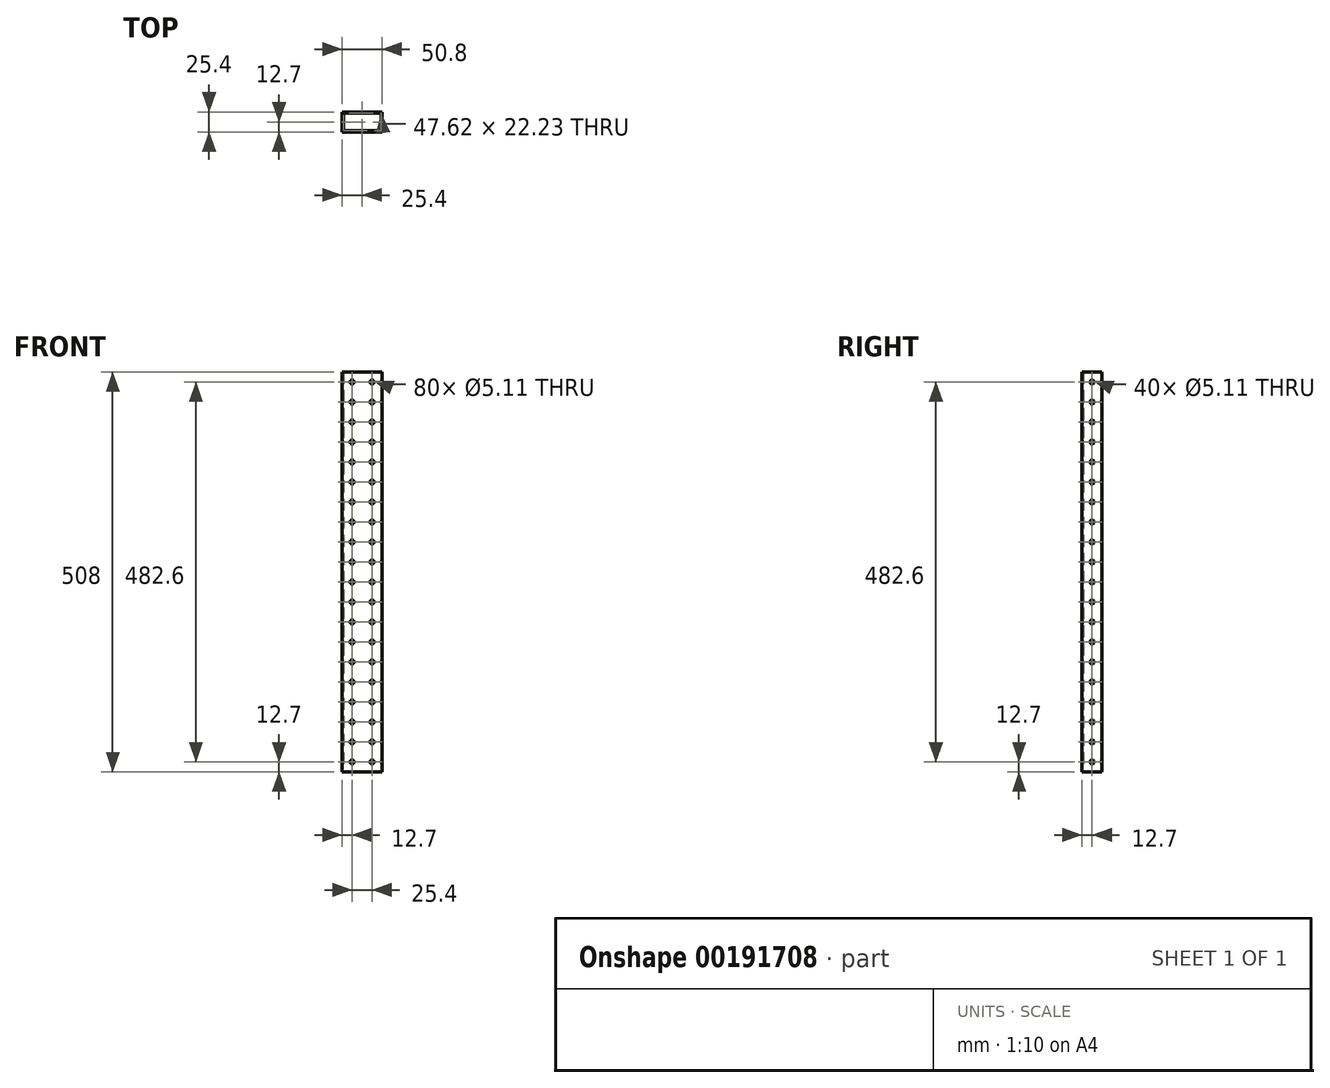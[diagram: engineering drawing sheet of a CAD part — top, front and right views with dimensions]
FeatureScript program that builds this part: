
annotation { "Feature Type Name" : "Feature", "Feature Type Description" : "" }
export const myFeature = defineFeature(function(context is Context, id is Id, definition is map)
    precondition{}
    {
        {
            var Q0;
            Q0=qCreatedBy(makeId("Top.planeOp"),FACE);
            var sketch = newSketch(context, id + "F0", { "sketchPlane" : qUnion([Q0])});
            skLineSegment(sketch, "E0.bottom", {"start": v(25.4, 12.7) * mm, "end": v(-25.4, 12.7) * mm});
            skLineSegment(sketch, "E0.top", {"start": v(25.4, -12.7) * mm, "end": v(-25.4, -12.7) * mm});
            skLineSegment(sketch, "E0.left", {"start": v(25.4, 12.7) * mm, "end": v(25.4, -12.7) * mm});
            skLineSegment(sketch, "E0.right", {"start": v(-25.4, 12.7) * mm, "end": v(-25.4, -12.7) * mm});
            skPoint(sketch, "E0.middle", {"position": v(0, 0) * mm});
            skLineSegment(sketch, "E1.bottom", {"start": v(23.81, 11.11) * mm, "end": v(-23.81, 11.11) * mm});
            skLineSegment(sketch, "E1.top", {"start": v(23.81, -11.11) * mm, "end": v(-23.81, -11.11) * mm});
            skLineSegment(sketch, "E1.left", {"start": v(23.81, 11.11) * mm, "end": v(23.81, -11.11) * mm});
            skLineSegment(sketch, "E1.right", {"start": v(-23.81, 11.11) * mm, "end": v(-23.81, -11.11) * mm});
            skSolve(sketch);
        }
        {
            var Q0;
            Q0 = qSketchRegion(id + "F0", true);
            extrude(context, id + "F1", {"entities" : qUnion([Q0]), "depth" : 508 * mm});
        }
        {
            var Q0;
            Q0=makeQuery(id+"F1.opExtrude","SWEPT_FACE",FACE,{"disambiguationData":[OSD([sQuery(id+"F0.wireOp",EDGE,"E0.top")])]});
            var sketch = newSketch(context, id + "F2", { "sketchPlane" : qUnion([Q0])});
            skCircle(sketch, "E2", {"center": v(-12.7, 12.7) * mm, "radius": 9.36 * mm});
            skCircle(sketch, "E3.0.1.0", {"center": v(-12.7, 38.1) * mm, "radius": 9.36 * mm});
            skCircle(sketch, "E3.0.2.0", {"center": v(-12.7, 63.5) * mm, "radius": 9.36 * mm});
            skCircle(sketch, "E3.0.3.0", {"center": v(-12.7, 88.9) * mm, "radius": 9.36 * mm});
            skCircle(sketch, "E3.0.4.0", {"center": v(-12.7, 114.3) * mm, "radius": 9.36 * mm});
            skCircle(sketch, "E3.0.5.0", {"center": v(-12.7, 139.7) * mm, "radius": 9.36 * mm});
            skCircle(sketch, "E3.0.6.0", {"center": v(-12.7, 165.1) * mm, "radius": 9.36 * mm});
            skCircle(sketch, "E3.0.7.0", {"center": v(-12.7, 190.5) * mm, "radius": 9.36 * mm});
            skCircle(sketch, "E3.0.8.0", {"center": v(-12.7, 215.9) * mm, "radius": 9.36 * mm});
            skCircle(sketch, "E3.0.9.0", {"center": v(-12.7, 241.3) * mm, "radius": 9.36 * mm});
            skCircle(sketch, "E3.0.10.0", {"center": v(-12.7, 266.7) * mm, "radius": 9.36 * mm});
            skCircle(sketch, "E3.0.11.0", {"center": v(-12.7, 292.1) * mm, "radius": 9.36 * mm});
            skCircle(sketch, "E3.0.12.0", {"center": v(-12.7, 317.5) * mm, "radius": 9.36 * mm});
            skCircle(sketch, "E3.0.13.0", {"center": v(-12.7, 342.9) * mm, "radius": 9.36 * mm});
            skCircle(sketch, "E3.0.14.0", {"center": v(-12.7, 368.3) * mm, "radius": 9.36 * mm});
            skCircle(sketch, "E3.0.15.0", {"center": v(-12.7, 393.7) * mm, "radius": 9.36 * mm});
            skCircle(sketch, "E3.0.16.0", {"center": v(-12.7, 419.1) * mm, "radius": 9.36 * mm});
            skCircle(sketch, "E3.0.17.0", {"center": v(-12.7, 444.5) * mm, "radius": 9.36 * mm});
            skCircle(sketch, "E3.0.18.0", {"center": v(-12.7, 469.9) * mm, "radius": 9.36 * mm});
            skCircle(sketch, "E3.1.0.0", {"center": v(12.7, 12.7) * mm, "radius": 9.36 * mm});
            skCircle(sketch, "E3.1.1.0", {"center": v(12.7, 38.1) * mm, "radius": 9.36 * mm});
            skCircle(sketch, "E3.1.2.0", {"center": v(12.7, 63.5) * mm, "radius": 9.36 * mm});
            skCircle(sketch, "E3.1.3.0", {"center": v(12.7, 88.9) * mm, "radius": 9.36 * mm});
            skCircle(sketch, "E3.1.4.0", {"center": v(12.7, 114.3) * mm, "radius": 9.36 * mm});
            skCircle(sketch, "E3.1.5.0", {"center": v(12.7, 139.7) * mm, "radius": 9.36 * mm});
            skCircle(sketch, "E3.1.6.0", {"center": v(12.7, 165.1) * mm, "radius": 9.36 * mm});
            skCircle(sketch, "E3.1.7.0", {"center": v(12.7, 190.5) * mm, "radius": 9.36 * mm});
            skCircle(sketch, "E3.1.8.0", {"center": v(12.7, 215.9) * mm, "radius": 9.36 * mm});
            skCircle(sketch, "E3.1.9.0", {"center": v(12.7, 241.3) * mm, "radius": 9.36 * mm});
            skCircle(sketch, "E3.1.10.0", {"center": v(12.7, 266.7) * mm, "radius": 9.36 * mm});
            skCircle(sketch, "E3.1.11.0", {"center": v(12.7, 292.1) * mm, "radius": 9.36 * mm});
            skCircle(sketch, "E3.1.12.0", {"center": v(12.7, 317.5) * mm, "radius": 9.36 * mm});
            skCircle(sketch, "E3.1.13.0", {"center": v(12.7, 342.9) * mm, "radius": 9.36 * mm});
            skCircle(sketch, "E3.1.14.0", {"center": v(12.7, 368.3) * mm, "radius": 9.36 * mm});
            skCircle(sketch, "E3.1.15.0", {"center": v(12.7, 393.7) * mm, "radius": 9.36 * mm});
            skCircle(sketch, "E3.1.16.0", {"center": v(12.7, 419.1) * mm, "radius": 9.36 * mm});
            skCircle(sketch, "E3.1.17.0", {"center": v(12.7, 444.5) * mm, "radius": 9.36 * mm});
            skCircle(sketch, "E3.1.18.0", {"center": v(12.7, 469.9) * mm, "radius": 9.36 * mm});
            skLineSegment(sketch, "E3.direction1", {"start": v(-12.7, 12.7) * mm, "end": v(12.7, 12.7) * mm, "construction": true});
            skLineSegment(sketch, "E3.direction2", {"start": v(-12.7, 12.7) * mm, "end": v(-12.7, 38.1) * mm, "construction": true});
            skCircle(sketch, "E4.0.0.19", {"center": v(-12.7, 495.3) * mm, "radius": 9.36 * mm});
            skCircle(sketch, "E4.0.1.19", {"center": v(12.7, 495.3) * mm, "radius": 9.36 * mm});
            skSolve(sketch);
        }
        {
            var Q0;
            Q0=sQuery(id+"F2.wireOp",VERTEX,"E3.0.12.0.center");
            var Q1;
            Q1=sQuery(id+"F2.wireOp",VERTEX,"E3.0.13.0.center");
            var Q2;
            Q2=sQuery(id+"F2.wireOp",VERTEX,"E3.1.13.0.center");
            var Q3;
            Q3=sQuery(id+"F2.wireOp",VERTEX,"E3.1.12.0.center");
            var Q4;
            Q4=sQuery(id+"F2.wireOp",VERTEX,"E3.1.11.0.center");
            var Q5;
            Q5=sQuery(id+"F2.wireOp",VERTEX,"E3.1.10.0.center");
            var Q6;
            Q6=sQuery(id+"F2.wireOp",VERTEX,"E3.0.10.0.center");
            var Q7;
            Q7=sQuery(id+"F2.wireOp",VERTEX,"E3.0.11.0.center");
            var Q8;
            Q8=sQuery(id+"F2.wireOp",VERTEX,"E3.1.4.0.center");
            var Q9;
            Q9=sQuery(id+"F2.wireOp",VERTEX,"E3.0.4.0.center");
            var Q10;
            Q10=sQuery(id+"F2.wireOp",VERTEX,"E3.0.5.0.center");
            var Q11;
            Q11=sQuery(id+"F2.wireOp",VERTEX,"E3.1.5.0.center");
            var Q12;
            Q12=sQuery(id+"F2.wireOp",VERTEX,"E3.1.6.0.center");
            var Q13;
            Q13=sQuery(id+"F2.wireOp",VERTEX,"E3.0.6.0.center");
            var Q14;
            Q14=sQuery(id+"F2.wireOp",VERTEX,"E3.0.7.0.center");
            var Q15;
            Q15=sQuery(id+"F2.wireOp",VERTEX,"E3.1.7.0.center");
            var Q16;
            Q16=sQuery(id+"F2.wireOp",VERTEX,"E3.0.8.0.center");
            var Q17;
            Q17=sQuery(id+"F2.wireOp",VERTEX,"E3.1.9.0.center");
            var Q18;
            Q18=sQuery(id+"F2.wireOp",VERTEX,"E3.0.9.0.center");
            var Q19;
            Q19=sQuery(id+"F2.wireOp",VERTEX,"E3.1.8.0.center");
            var Q20;
            Q20=sQuery(id+"F2.wireOp",VERTEX,"E3.0.16.0.center");
            var Q21;
            Q21=sQuery(id+"F2.wireOp",VERTEX,"E3.0.18.0.center");
            var Q22;
            Q22=sQuery(id+"F2.wireOp",VERTEX,"E3.1.18.0.center");
            var Q23;
            Q23=sQuery(id+"F2.wireOp",VERTEX,"E3.1.16.0.center");
            var Q24;
            Q24=sQuery(id+"F2.wireOp",VERTEX,"E3.1.17.0.center");
            var Q25;
            Q25=sQuery(id+"F2.wireOp",VERTEX,"E3.0.17.0.center");
            var Q26;
            Q26=sQuery(id+"F2.wireOp",VERTEX,"E3.0.15.0.center");
            var Q27;
            Q27=sQuery(id+"F2.wireOp",VERTEX,"E3.1.15.0.center");
            var Q28;
            Q28=sQuery(id+"F2.wireOp",VERTEX,"E3.1.14.0.center");
            var Q29;
            Q29=sQuery(id+"F2.wireOp",VERTEX,"E3.0.14.0.center");
            var Q30;
            Q30=sQuery(id+"F2.wireOp",VERTEX,"E3.1.2.0.center");
            var Q31;
            Q31=sQuery(id+"F2.wireOp",VERTEX,"E3.1.3.0.center");
            var Q32;
            Q32=sQuery(id+"F2.wireOp",VERTEX,"E3.direction1.end");
            var Q33;
            Q33=sQuery(id+"F2.wireOp",VERTEX,"E3.1.1.0.center");
            var Q34;
            Q34=sQuery(id+"F2.wireOp",VERTEX,"E2.center");
            var Q35;
            Q35=sQuery(id+"F2.wireOp",VERTEX,"E3.0.1.0.center");
            var Q36;
            Q36=sQuery(id+"F2.wireOp",VERTEX,"E3.0.2.0.center");
            var Q37;
            Q37=sQuery(id+"F2.wireOp",VERTEX,"E3.0.3.0.center");
            var Q38;
            Q38=sQuery(id+"F2.wireOp",VERTEX,"E4.0.0.19.center");
            var Q39;
            Q39=sQuery(id+"F2.wireOp",VERTEX,"E4.0.1.19.center");
            var Q40;
            Q40=makeQuery(id+"F1.opExtrude","SWEPT_BODY",BODY,{"disambiguationData":[OSD([sQuery(id+"F0.wireOp",EDGE,"E0.bottom"),sQuery(id+"F0.wireOp",EDGE,"E0.top"),sQuery(id+"F0.wireOp",EDGE,"E0.left"),sQuery(id+"F0.wireOp",EDGE,"E0.right"),sQuery(id+"F0.wireOp",EDGE,"E1.bottom"),sQuery(id+"F0.wireOp",EDGE,"E1.top"),sQuery(id+"F0.wireOp",EDGE,"E1.left"),sQuery(id+"F0.wireOp",EDGE,"E1.right")])]});
            hole(context, id + "F3", {"style" : HoleStyle.SIMPLE, "endStyle" : HoleEndStyle.THROUGH, "holeDiameter" : 5.1 * mm, "tappedDepth" : 12.7 * mm, "tapClearance" : 3, "locations" : qUnion([Q0, Q1, Q2, Q3, Q4, Q5, Q6, Q7, Q8, Q9, Q10, Q11, Q12, Q13, Q14, Q15, Q16, Q17, Q18, Q19, Q20, Q21, Q22, Q23, Q24, Q25, Q26, Q27, Q28, Q29, Q30, Q31, Q32, Q33, Q34, Q35, Q36, Q37, Q38, Q39]), "scope" : qUnion([Q40])});
        }
        {
            var Q0;
            Q0=makeQuery(id+"F1.opExtrude","SWEPT_FACE",FACE,{"disambiguationData":[OSD([sQuery(id+"F0.wireOp",EDGE,"E0.left")])]});
            var sketch = newSketch(context, id + "F4", { "sketchPlane" : qUnion([Q0])});
            skCircle(sketch, "E5", {"center": v(0, 12.7) * mm, "radius": 9.57 * mm});
            skCircle(sketch, "E6.0.1.0", {"center": v(0, 38.1) * mm, "radius": 9.57 * mm});
            skCircle(sketch, "E6.0.2.0", {"center": v(0, 63.5) * mm, "radius": 9.57 * mm});
            skCircle(sketch, "E6.0.3.0", {"center": v(0, 88.9) * mm, "radius": 9.57 * mm});
            skCircle(sketch, "E6.0.4.0", {"center": v(0, 114.3) * mm, "radius": 9.57 * mm});
            skCircle(sketch, "E6.0.5.0", {"center": v(0, 139.7) * mm, "radius": 9.57 * mm});
            skCircle(sketch, "E6.0.6.0", {"center": v(0, 165.1) * mm, "radius": 9.57 * mm});
            skCircle(sketch, "E6.0.7.0", {"center": v(0, 190.5) * mm, "radius": 9.57 * mm});
            skCircle(sketch, "E6.0.8.0", {"center": v(0, 215.9) * mm, "radius": 9.57 * mm});
            skCircle(sketch, "E6.0.9.0", {"center": v(0, 241.3) * mm, "radius": 9.57 * mm});
            skCircle(sketch, "E6.0.10.0", {"center": v(0, 266.7) * mm, "radius": 9.57 * mm});
            skCircle(sketch, "E6.0.11.0", {"center": v(0, 292.1) * mm, "radius": 9.57 * mm});
            skCircle(sketch, "E6.0.12.0", {"center": v(0, 317.5) * mm, "radius": 9.57 * mm});
            skCircle(sketch, "E6.0.13.0", {"center": v(0, 342.9) * mm, "radius": 9.57 * mm});
            skCircle(sketch, "E6.0.14.0", {"center": v(0, 368.3) * mm, "radius": 9.57 * mm});
            skCircle(sketch, "E6.0.15.0", {"center": v(0, 393.7) * mm, "radius": 9.57 * mm});
            skCircle(sketch, "E6.0.16.0", {"center": v(0, 419.1) * mm, "radius": 9.57 * mm});
            skCircle(sketch, "E6.0.17.0", {"center": v(0, 444.5) * mm, "radius": 9.57 * mm});
            skCircle(sketch, "E6.0.18.0", {"center": v(0, 469.9) * mm, "radius": 9.57 * mm});
            skLineSegment(sketch, "E6.direction1", {"start": v(0, 12.7) * mm, "end": v(25.4, 12.7) * mm, "construction": true});
            skLineSegment(sketch, "E6.direction2", {"start": v(0, 12.7) * mm, "end": v(0, 38.1) * mm, "construction": true});
            skCircle(sketch, "E7.0.0.19", {"center": v(0, 495.3) * mm, "radius": 9.57 * mm});
            skSolve(sketch);
        }
        {
            var Q0;
            Q0=sQuery(id+"F4.wireOp",VERTEX,"E6.0.1.0.center");
            var Q1;
            Q1=sQuery(id+"F4.wireOp",VERTEX,"E5.center");
            var Q2;
            Q2=sQuery(id+"F4.wireOp",VERTEX,"E6.0.3.0.center");
            var Q3;
            Q3=sQuery(id+"F4.wireOp",VERTEX,"E6.0.2.0.center");
            var Q4;
            Q4=sQuery(id+"F4.wireOp",VERTEX,"E6.0.8.0.center");
            var Q5;
            Q5=sQuery(id+"F4.wireOp",VERTEX,"E6.0.7.0.center");
            var Q6;
            Q6=sQuery(id+"F4.wireOp",VERTEX,"E6.0.6.0.center");
            var Q7;
            Q7=sQuery(id+"F4.wireOp",VERTEX,"E6.0.5.0.center");
            var Q8;
            Q8=sQuery(id+"F4.wireOp",VERTEX,"E6.0.4.0.center");
            var Q9;
            Q9=sQuery(id+"F4.wireOp",VERTEX,"E6.0.17.0.center");
            var Q10;
            Q10=sQuery(id+"F4.wireOp",VERTEX,"E6.0.18.0.center");
            var Q11;
            Q11=sQuery(id+"F4.wireOp",VERTEX,"E6.0.16.0.center");
            var Q12;
            Q12=sQuery(id+"F4.wireOp",VERTEX,"E6.0.12.0.center");
            var Q13;
            Q13=sQuery(id+"F4.wireOp",VERTEX,"E6.0.13.0.center");
            var Q14;
            Q14=sQuery(id+"F4.wireOp",VERTEX,"E6.0.14.0.center");
            var Q15;
            Q15=sQuery(id+"F4.wireOp",VERTEX,"E6.0.15.0.center");
            var Q16;
            Q16=sQuery(id+"F4.wireOp",VERTEX,"E6.0.10.0.center");
            var Q17;
            Q17=sQuery(id+"F4.wireOp",VERTEX,"E6.0.11.0.center");
            var Q18;
            Q18=sQuery(id+"F4.wireOp",VERTEX,"E6.0.9.0.center");
            var Q19;
            Q19=sQuery(id+"F4.wireOp",VERTEX,"E7.0.0.19.center");
            var Q20;
            Q20=makeQuery(id+"F1.opExtrude","SWEPT_BODY",BODY,{"disambiguationData":[OSD([sQuery(id+"F0.wireOp",EDGE,"E0.bottom"),sQuery(id+"F0.wireOp",EDGE,"E0.top"),sQuery(id+"F0.wireOp",EDGE,"E0.left"),sQuery(id+"F0.wireOp",EDGE,"E0.right"),sQuery(id+"F0.wireOp",EDGE,"E1.bottom"),sQuery(id+"F0.wireOp",EDGE,"E1.top"),sQuery(id+"F0.wireOp",EDGE,"E1.left"),sQuery(id+"F0.wireOp",EDGE,"E1.right")])]});
            hole(context, id + "F5", {"style" : HoleStyle.SIMPLE, "endStyle" : HoleEndStyle.THROUGH, "holeDiameter" : 5.1 * mm, "tappedDepth" : 12.7 * mm, "tapClearance" : 3, "locations" : qUnion([Q0, Q1, Q2, Q3, Q4, Q5, Q6, Q7, Q8, Q9, Q10, Q11, Q12, Q13, Q14, Q15, Q16, Q17, Q18, Q19]), "scope" : qUnion([Q20])});
        }
    });
